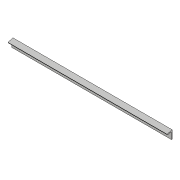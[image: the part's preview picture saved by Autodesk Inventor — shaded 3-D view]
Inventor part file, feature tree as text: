
AUTODESK INVENTOR PART (.ipt)
format: ipt  version: 2022 (Build 260153000, 153)  size: 109,568 bytes
history: native  units: in
note: dims shown in document units (in); Inventor stores cm internally (conversion verified against a paired STEP export)
features: sketch x2, revolve x2, extrude x1, hole x1, pattern_linear x1, direct_edit x1, chamfer x1
ambient origin geometry x8: Origin, YZ Plane, XZ Plane, XY Plane, X Axis, Y Axis, Z Axis, Center Point
bodies: Body1 (feature_tree)
feature tree (9):
  extrude  "Extrusion2"  Depth=0.0787in
  hole  "Hole1"  [1 undecoded]
  pattern_linear  "Rectangular Pattern1"  Spacing1=0.0in  [1 undecoded]
  direct_edit  "Direct Edit1"
  chamfer  "Chamfer1"  Distance=0.9843in
  sketch  "Sketch3"  dims[d4=0.0787in d5=0.4331in]
  sketch  "Sketch4"  dims[d6=0.0787in d7=0.7087in d9=0.0in d10=0.9843in d12=0.1339in d13=0.2362in d14=0.248in d15=0.0787in d16=90.0deg d17=0.315in d18=0.8108in d19=1.1811in d21=11.4173in d22=90.0deg d23=90.0deg d24=0.0394in d25=0.0787in d26=45.0deg d27=0.3937in]
  revolve  "Rotate1"  [1 undecoded]
  revolve  "Rotate2"  Angle=90.0deg
note: 3 required parameter values undecoded (feature->parameter linkage not recoverable at this tier; creation-order binding heuristic only, values carry confidence <= 0.55)